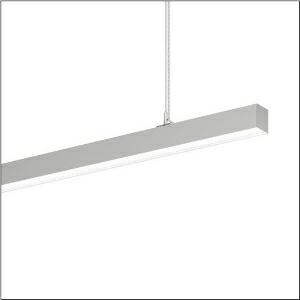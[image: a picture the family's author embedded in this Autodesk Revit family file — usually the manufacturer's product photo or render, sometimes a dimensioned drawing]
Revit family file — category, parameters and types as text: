
# Revit family: silica_21_51mx30tat4s
name_source: partatom
category: Lighting Fixtures
units: mm (PartAtom-declared; Revit-internal decimal feet)

## family parameters
Cut with Voids When Loaded = No
Host = Face
Light Source = No
Part Type = Normal
Room Calculation Point = No
Round Connector Dimension = Use Diameter
Shared = No

## types (1)
- --- (1 x LED, 4120 lm, 33.8 W, 6500K)
    Apparent Load = 34 VA
    CIE Flux Codes = 47 79 96 58 100
    Color Rendering = 80
    Color Temperature = 6500K
    Default Elevation = 1800 mm
    Description = Silica 21, office luminaire, primary optical cover: cover, of PMMA, opal, light emission: direct/indirect distribution, primary light characteristic: symmetric, installation type: suspended mounting, LED, rated luminous flux: 4.120lm, luminous efficacy: 116lm/W, light colour: 8tw, colour temperature: 2700..6500K, control gear: DALI DT8, with terminal, 3+2-pole, max. 2.5mm², mains connection: 220..240V, AC, 50/60Hz, rated input power: 35.5W, luminaire housing, of aluminium, metallic grey (RAL 9006), length: 1.204mm, width: 53mm, height: 53mm, protection rating (complete): IP20, insulation class (complete): insulation class I (protective earthing), certification: CE, permissible operating ambient temperature: 0..+35°C, standard: EN 50419, packaging unit: 1 piece
    Height = 53 mm
    Lamp = 1 x LED
    Lamp Light Flux = 4120 lm
    Lamp Power = 33.8 W
    Lamp count = 1
    Length = 1204 mm
    Luminous efficacy = 122 lm/W
    Manufacturer = Siteco
    ModVariant = No
    Model = 51MX30TAT4S
    Mounting Place = Ceiling
    Mounting Type = Pendant
    Number of Poles = 1
    OnlyDefault = Yes
    Power Factor = 1
    Product Name = Silica 21
    Product group = office luminaire | ceiling pendant
    ProductGroupID = 903
    Protection Class = Protection class I
    Protection Degree = IP 20
    RLX_Detail_Level = 1
    RLX_Emergency_Light_Flux = 0 lm
    RLX_Emergency_Type = 0
    RLX_Emergency_Type_DB = No
    RlxData = <blob elided: 20089 chars, md5=72a086f0>
    Socket = socket
    Standby Power = 0 W
    System Light Flux = 4120 lm
    System Power = 34 W
    Type Comments = individual setting
    Type Image = l_1335864.jpg
    URL = http://relux.com
    VarID = @adj_139115
    Voltage = 0 V
    Weight = 0.00 kg
    Width = 53 mm

## geometry (parser evidence)
native form markers: Blend x4, Sweep x14
no freeform markers — native parametric forms only
